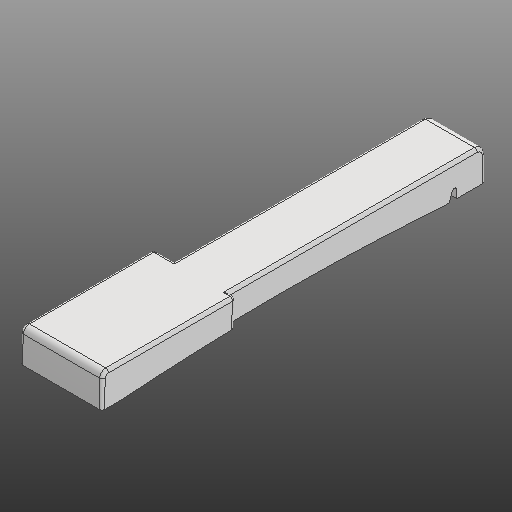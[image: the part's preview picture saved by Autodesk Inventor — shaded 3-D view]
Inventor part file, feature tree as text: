
AUTODESK INVENTOR PART (.ipt)
format: ipt  version: 2020 (Build 240168000, 168)  size: 325,632 bytes
history: native  units: in
note: dims shown in document units (in); Inventor stores cm internally (conversion verified against a paired STEP export)
features: extrude x4, other x3, fillet x2
ambient origin geometry x8: Origin, YZ Plane, XZ Plane, XY Plane, X Axis, Y Axis, Z Axis, Center Point
bodies: Solid1 (feature_tree)
feature tree (9):
  other  "Slot Start Plane"
  other  "Key Profile"
  extrude  "Upper (u)"  TaperAngle=0.0deg  [1 undecoded]
  extrude  "Lower (d)"  TaperAngle=0.0deg  [1 undecoded]
  extrude  "Protrusion Cutout"  Depth=0.0591in
  fillet  "Front Fillet"  Radius=0.1374in
  extrude  "Slot"  [1 undecoded]
  fillet  "Edge Softening"  Radius=0.0787in
  other  "Slot Sketch"
note: 3 required parameter values undecoded (feature->parameter linkage not recoverable at this tier; creation-order binding heuristic only, values carry confidence <= 0.55)
